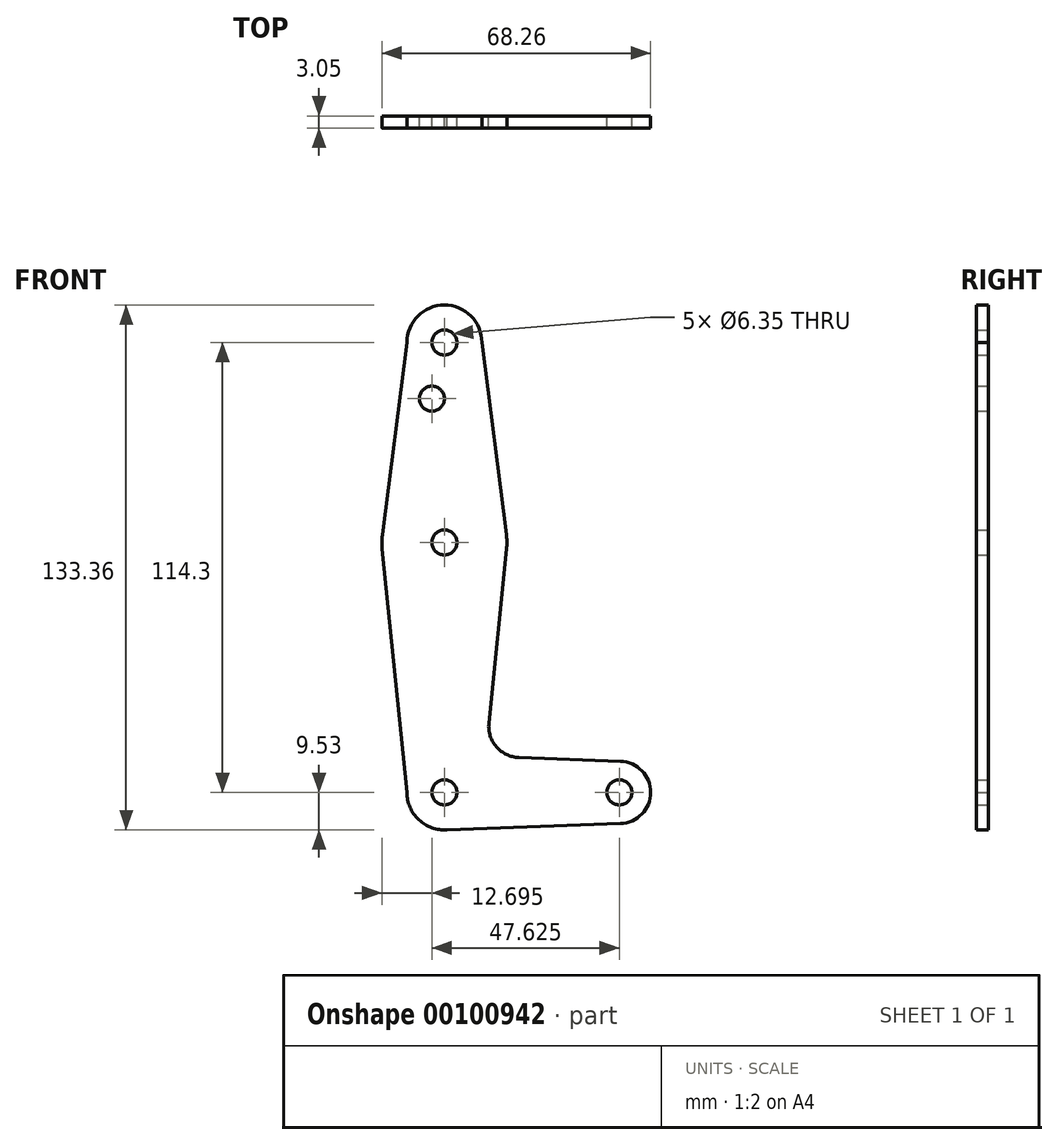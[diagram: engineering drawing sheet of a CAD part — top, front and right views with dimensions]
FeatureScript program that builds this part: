
annotation { "Feature Type Name" : "Feature", "Feature Type Description" : "" }
export const myFeature = defineFeature(function(context is Context, id is Id, definition is map)
    precondition{}
    {
        {
            var Q0;
            Q0=qCreatedBy(makeId("Front.planeOp"),FACE);
            var sketch = newSketch(context, id + "F0", { "sketchPlane" : qUnion([Q0])});
            skLineSegment(sketch, "E0", {"start": v(0, 0) * mm, "end": v(0, 114.3) * mm, "construction": true});
            skLineSegment(sketch, "E1", {"start": v(0, 0) * mm, "end": v(44.45, 0) * mm, "construction": true});
            skCircle(sketch, "E2", {"center": v(0, 114.3) * mm, "radius": 9.53 * mm});
            skCircle(sketch, "E3", {"center": v(0, 63.5) * mm, "radius": 15.88 * mm});
            skCircle(sketch, "E4", {"center": v(0, 0) * mm, "radius": 9.53 * mm});
            skCircle(sketch, "E5", {"center": v(44.45, 0) * mm, "radius": 7.94 * mm});
            skLineSegment(sketch, "E6", {"start": v(-15.75, 65.5) * mm, "end": v(-9.52, 114.3) * mm});
            skLineSegment(sketch, "E7", {"start": v(15.75, 65.5) * mm, "end": v(9.52, 114.3) * mm});
            skLineSegment(sketch, "E8", {"start": v(-15.8, 61.9) * mm, "end": v(-9.53, 0) * mm});
            skLineSegment(sketch, "E9", {"start": v(15.8, 61.9) * mm, "end": v(11.3, 17.6) * mm});
            skLineSegment(sketch, "E10", {"start": v(18.93, 8.85) * mm, "end": v(44.73, 7.93) * mm});
            skLineSegment(sketch, "E11", {"start": v(0, -9.53) * mm, "end": v(44.73, -7.93) * mm});
            skCircle(sketch, "E12", {"center": v(0, 114.3) * mm, "radius": 3.18 * mm});
            skCircle(sketch, "E13", {"center": v(-3.18, 100.03) * mm, "radius": 3.18 * mm});
            skCircle(sketch, "E14", {"center": v(0, 63.5) * mm, "radius": 3.18 * mm});
            skCircle(sketch, "E15", {"center": v(0, 0) * mm, "radius": 3.18 * mm});
            skCircle(sketch, "E16", {"center": v(44.45, 0) * mm, "radius": 3.18 * mm});
            skPoint(sketch, "E17.newPointA", {"position": v(9.52, 0) * mm});
            skArc(sketch, "E17.filletArc", {"start": v(11.3, 17.6) * mm, "mid": v(13.22, 11.57) * mm, "end": v(18.93, 8.85) * mm});
            skSolve(sketch);
        }
        {
            var Q0;
            Q0 = qSketchRegion(id + "F0", true);
            extrude(context, id + "F1", {"entities" : qUnion([Q0]), "depth" : 3.05 * mm});
        }
    });
